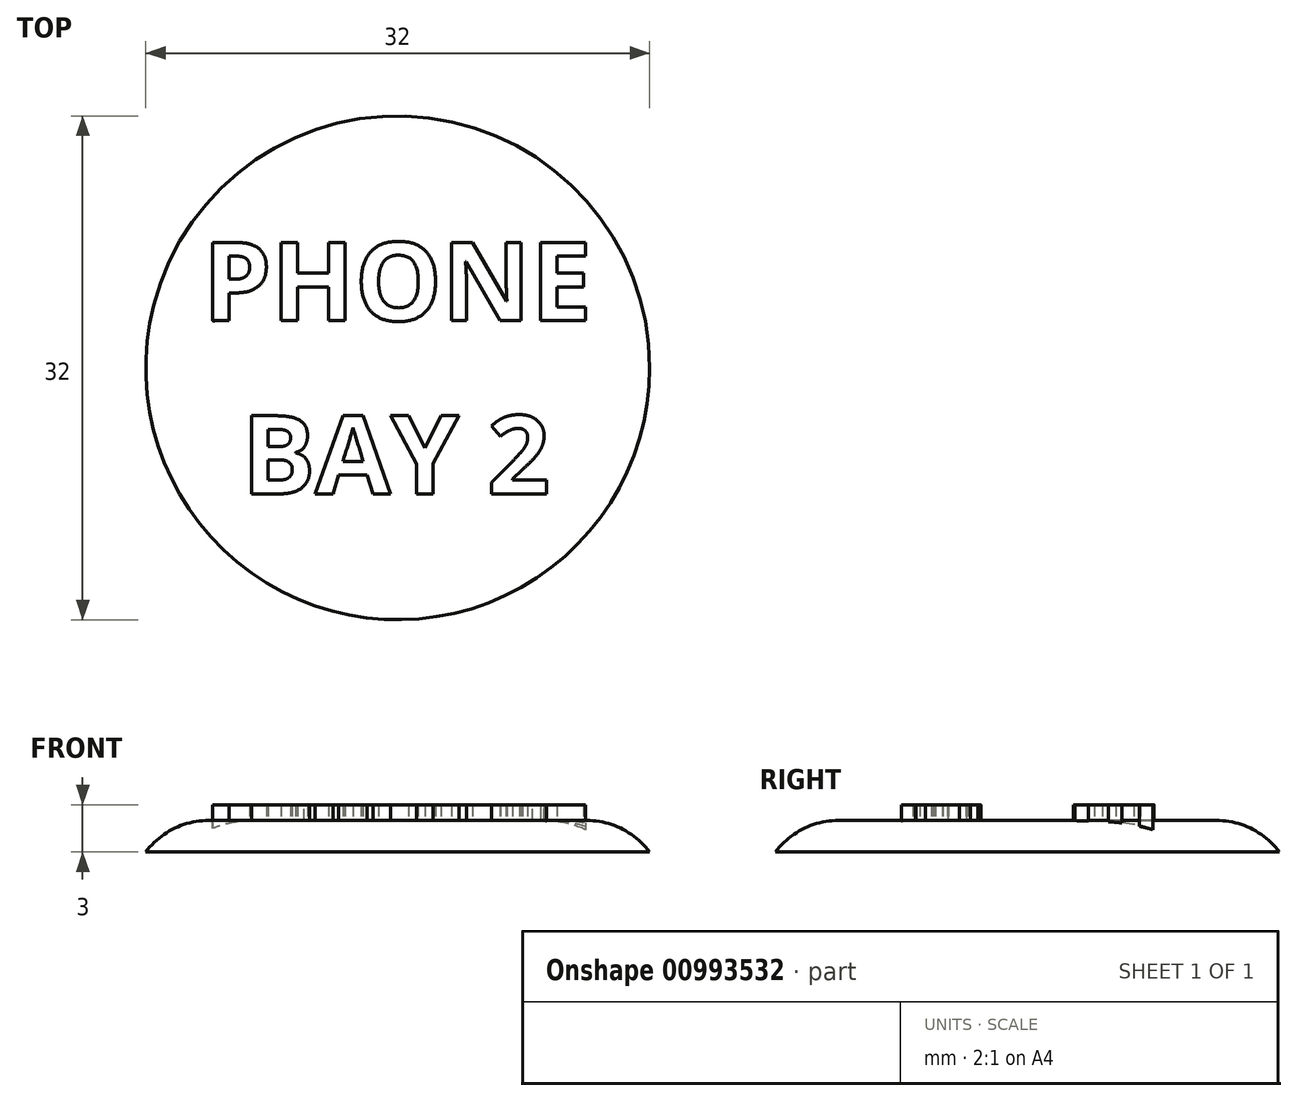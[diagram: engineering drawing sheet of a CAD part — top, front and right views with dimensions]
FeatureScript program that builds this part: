
annotation { "Feature Type Name" : "Feature", "Feature Type Description" : "" }
export const myFeature = defineFeature(function(context is Context, id is Id, definition is map)
    precondition{}
    {
        {
            var Q0;
            Q0=qCreatedBy(makeId("Top.planeOp"),FACE);
            var sketch = newSketch(context, id + "F0", { "sketchPlane" : qUnion([Q0])});
            skCircle(sketch, "E0", {"center": v(0, 0) * mm, "radius": 16 * mm});
            skSolve(sketch);
        }
        {
            var Q0;
            Q0=qSketchRegion(id+"F0",true);
            extrude(context, id + "F1", {"entities" : qUnion([Q0]), "depth" : 2 * mm, "offsetDistance" : 25 * mm});
        }
        {
            var Q0;
            Q0=makeQuery(id+"F1.opExtrude","CAP_FACE",FACE,{"disambiguationData":[OSD([sQuery(id+"F0.wireOp",EDGE,"E0")])],"isStart":false});
            var sketch = newSketch(context, id + "F2", { "sketchPlane" : qUnion([Q0])});
            skText(sketch, "E1", { "text": "PHONE", "fontName": "OpenSans-Bold.ttf"});
            skText(sketch, "E2", { "text": "BAY 2", "fontName": "OpenSans-Bold.ttf"});
            skLineSegment(sketch, "E3", {"start": v(0, -3) * mm, "end": v(0, 0) * mm, "construction": true});
            skLineSegment(sketch, "E4", {"start": v(0, 0) * mm, "end": v(0, 3) * mm, "construction": true});
            const initialGuessF2  = {"E1": [-0.01239, 0.003, 1, 0, 0.005], "E2": [-0.0099, -0.008, 1, 0, 0.005]};
            skSetInitialGuess(sketch, initialGuessF2);
            skSolve(sketch);
        }
        {
            var Q0;
            Q0=qSketchRegion(id+"F2",true);
            extrude(context, id + "F3", {"entities" : qUnion([Q0]), "operationType" : NewBodyOperationType.ADD, "depth" : 1 * mm, "offsetDistance" : 25 * mm});
        }
        {
            var Q0;
            Q0=makeQuery(id+"F1.opExtrude","CAP_EDGE",EDGE,{"disambiguationData":[OSD([sQuery(id+"F0.wireOp",EDGE,"E0")])],"isStart":false});
            fillet(context, id + "F4", {"entities" : qUnion([Q0]), "radius" : 5 * mm, "tangentPropagation" : true, "allowEdgeOverflow" : false});
        }
    });
